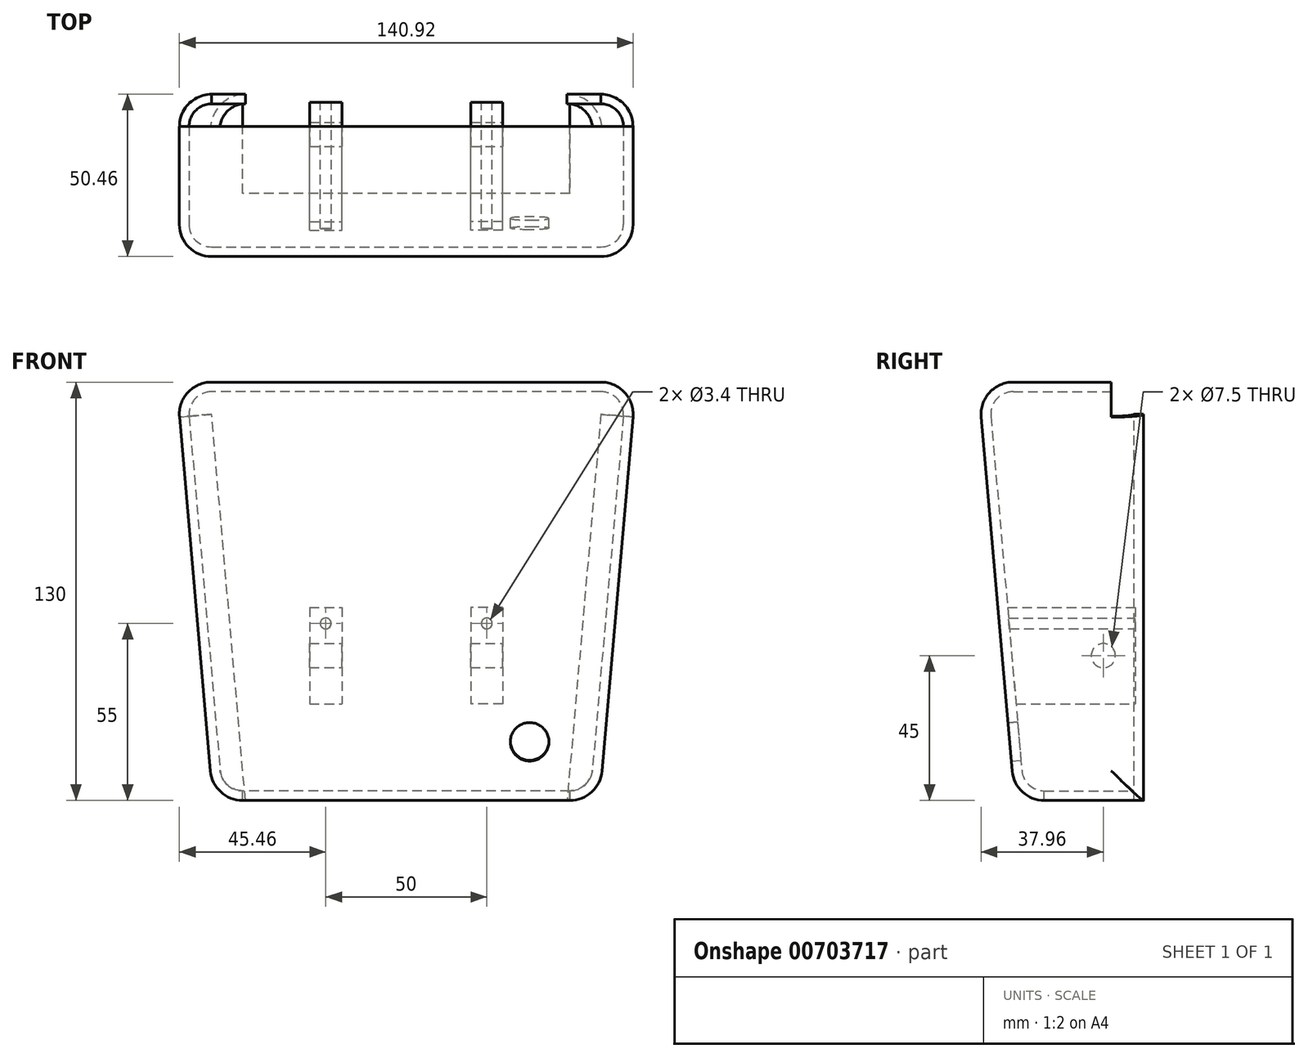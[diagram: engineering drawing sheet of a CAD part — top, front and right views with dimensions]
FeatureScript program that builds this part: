
annotation { "Feature Type Name" : "Feature", "Feature Type Description" : "" }
export const myFeature = defineFeature(function(context is Context, id is Id, definition is map)
    precondition{}
    {
        {
            var Q0;
            Q0=qCreatedBy(makeId("Top.planeOp"),FACE);
            var sketch = newSketch(context, id + "F0", { "sketchPlane" : qUnion([Q0])});
            skLineSegment(sketch, "E0.bottom", {"start": v(0, 0) * mm, "end": v(120, 0) * mm});
            skLineSegment(sketch, "E0.top", {"start": v(0, -40) * mm, "end": v(120, -40) * mm});
            skLineSegment(sketch, "E0.left", {"start": v(0, 0) * mm, "end": v(0, -40) * mm});
            skLineSegment(sketch, "E0.right", {"start": v(120, 0) * mm, "end": v(120, -40) * mm});
            skPoint(sketch, "E1", {"position": v(120, 0) * mm});
            skLineSegment(sketch, "E2", {"start": v(120, 0) * mm, "end": v(120, -47.34) * mm, "construction": true});
            skPoint(sketch, "E3.visualSharp", {"position": v(120, -40) * mm});
            skLineSegment(sketch, "E3.filletArc", {"start": v(120, -40) * mm, "end": v(120, -40) * mm});
            skLineSegment(sketch, "E4.filletArc", {"start": v(120, 0) * mm, "end": v(120, 0) * mm});
            skPoint(sketch, "E5.visualSharp", {"position": v(0, 0) * mm});
            skLineSegment(sketch, "E5.filletArc", {"start": v(0, 0) * mm, "end": v(0, 0) * mm});
            skPoint(sketch, "E6.visualSharp", {"position": v(0, -40) * mm});
            skLineSegment(sketch, "E6.filletArc", {"start": v(0, -40) * mm, "end": v(0, -40) * mm});
            skSolve(sketch);
        }
        {
            var Q0;
            Q0 = qSketchRegion(id + "F0", true);
            extrude(context, id + "F1", {"entities" : qUnion([Q0]), "depth" : 130 * mm, "offsetDistance" : 25 * mm, "hasDraft" : true, "draftAngle" : 5 * degree});
        }
        {
            var Q0;
            Q0=qCreatedBy(makeId("Front.planeOp"),FACE);
            var sketch = newSketch(context, id + "F2", { "sketchPlane" : qUnion([Q0])});
            skLineSegment(sketch, "E7.bottom", {"start": v(146.84, 147.54) * mm, "end": v(-36.23, 147.54) * mm});
            skLineSegment(sketch, "E7.top", {"start": v(146.84, -9) * mm, "end": v(-36.23, -9) * mm});
            skLineSegment(sketch, "E7.left", {"start": v(146.84, 147.54) * mm, "end": v(146.84, -9) * mm});
            skLineSegment(sketch, "E7.right", {"start": v(-36.23, 147.54) * mm, "end": v(-36.23, -9) * mm});
            skPoint(sketch, "E7.middle", {"position": v(55.3, 69.27) * mm});
            skSolve(sketch);
        }
        {
            var Q0;
            Q0=makeQuery(id+"F2.imprint","IMPRINT",FACE,{"disambiguationData":[TD([[makeQuery(id+"F2.imprint","IMPRINT",EDGE,{"derivedFrom":sQuery(id+"F2.wireOp",EDGE,"E7.bottom")}),1.0]])]});
            extrude(context, id + "F3", {"entities" : qUnion([Q0]), "operationType" : NewBodyOperationType.REMOVE, "oppositeDirection" : true, "depth" : 150 * mm, "offsetDistance" : 25 * mm});
        }
        {
            var Q0;
            Q0=makeQuery(id+"F1.opExtrude","SWEPT_FACE",FACE,{"disambiguationData":[OSD([sQuery(id+"F0.wireOp",EDGE,"E0.right")])]});
            var Q1;
            Q1=makeQuery(id+"F1.opExtrude","SWEPT_FACE",FACE,{"disambiguationData":[OSD([sQuery(id+"F0.wireOp",EDGE,"E0.left")])]});
            var Q2;
            Q2=makeQuery(id+"F1.opExtrude","CAP_FACE",FACE,{"disambiguationData":[OSD([sQuery(id+"F0.wireOp",EDGE,"E0.bottom"),sQuery(id+"F0.wireOp",EDGE,"E0.top"),sQuery(id+"F0.wireOp",EDGE,"E0.left"),sQuery(id+"F0.wireOp",EDGE,"E0.right")])],"isStart":false});
            var Q3;
            Q3=makeQuery(id+"F1.opExtrude","CAP_EDGE",EDGE,{"disambiguationData":[OSD([sQuery(id+"F0.wireOp",EDGE,"E0.bottom")])],"isStart":true});
            var Q4;
            Q4=makeQuery(id+"F1.opExtrude","SWEPT_FACE",FACE,{"disambiguationData":[OSD([sQuery(id+"F0.wireOp",EDGE,"E0.top")])]});
            fillet(context, id + "F4", {"entities" : qUnion([Q0, Q1, Q2, Q3, Q4]), "radius" : 10 * mm, "tangentPropagation" : true, "allowEdgeOverflow" : false});
        }
        {
            var Q0;
            Q0=makeQuery(id+"F3.boolean.opBoolean","COPY",FACE,{"derivedFrom":makeQuery(id+"F3.opExtrude","CAP_FACE",FACE,{"disambiguationData":[OSD([sQuery(id+"F2.wireOp",EDGE,"E7.bottom"),sQuery(id+"F2.wireOp",EDGE,"E7.top"),sQuery(id+"F2.wireOp",EDGE,"E7.left"),sQuery(id+"F2.wireOp",EDGE,"E7.right")])],"isStart":true})});
            var Q1;
            Q1=makeQuery(id+"F1.opExtrude","CAP_FACE",FACE,{"disambiguationData":[OSD([sQuery(id+"F0.wireOp",EDGE,"E0.bottom"),sQuery(id+"F0.wireOp",EDGE,"E0.top"),sQuery(id+"F0.wireOp",EDGE,"E0.left"),sQuery(id+"F0.wireOp",EDGE,"E0.right")])],"isStart":true});
            var Q2;
            Q2=makeQuery(id+"F4.opFillet","BLEND_FACE",FACE,{"disambiguationData":[OSD([sQuery(id+"F0.wireOp",EDGE,"E0.bottom")])]});
            shell(context, id + "F5", {"entities" : qUnion([Q0, Q1, Q2]), "thickness" : 3 * mm});
        }
        {
            var Q0;
            Q0=makeQuery(id+"F2.imprint","IMPRINT",FACE,{"disambiguationData":[TD([[makeQuery(id+"F2.imprint","IMPRINT",EDGE,{"derivedFrom":sQuery(id+"F2.wireOp",EDGE,"E7.bottom")}),1.0]])]});
            var sketch = newSketch(context, id + "F6", { "sketchPlane" : qUnion([Q0])});
            skLineSegment(sketch, "E8.bottom", {"start": v(0, 0) * mm, "end": v(120, 0) * mm, "construction": true});
            skLineSegment(sketch, "E8.top", {"start": v(0, 50) * mm, "end": v(120, 50) * mm, "construction": true});
            skLineSegment(sketch, "E8.left", {"start": v(0, 0) * mm, "end": v(0, 50) * mm, "construction": true});
            skLineSegment(sketch, "E8.right", {"start": v(120, 0) * mm, "end": v(120, 50) * mm, "construction": true});
            skLineSegment(sketch, "E9.bottom", {"start": v(120, 50) * mm, "end": v(90, 50) * mm, "construction": true});
            skLineSegment(sketch, "E9.top", {"start": v(120, 60) * mm, "end": v(90, 60) * mm, "construction": true});
            skLineSegment(sketch, "E9.left", {"start": v(120, 50) * mm, "end": v(120, 60) * mm, "construction": true});
            skLineSegment(sketch, "E9.right", {"start": v(90, 50) * mm, "end": v(90, 60) * mm, "construction": true});
            skLineSegment(sketch, "E10.bottom", {"start": v(0, 50) * mm, "end": v(30, 50) * mm, "construction": true});
            skLineSegment(sketch, "E10.top", {"start": v(0, 60) * mm, "end": v(30, 60) * mm, "construction": true});
            skLineSegment(sketch, "E10.left", {"start": v(0, 50) * mm, "end": v(0, 60) * mm, "construction": true});
            skLineSegment(sketch, "E10.right", {"start": v(30, 50) * mm, "end": v(30, 60) * mm, "construction": true});
            skLineSegment(sketch, "E11.bottom", {"start": v(30, 60) * mm, "end": v(40, 60) * mm});
            skLineSegment(sketch, "E11.top", {"start": v(30, 30) * mm, "end": v(40, 30) * mm});
            skLineSegment(sketch, "E11.left", {"start": v(30, 60) * mm, "end": v(30, 30) * mm});
            skLineSegment(sketch, "E11.right", {"start": v(40, 60) * mm, "end": v(40, 30) * mm});
            skLineSegment(sketch, "E12.bottom", {"start": v(90, 60) * mm, "end": v(80, 60) * mm});
            skLineSegment(sketch, "E12.top", {"start": v(90, 30) * mm, "end": v(80, 30) * mm});
            skLineSegment(sketch, "E12.left", {"start": v(90, 60) * mm, "end": v(90, 30) * mm});
            skLineSegment(sketch, "E12.right", {"start": v(80, 60) * mm, "end": v(80, 30) * mm});
            skLineSegment(sketch, "E13.bottom", {"start": v(40, 60) * mm, "end": v(35, 60) * mm, "construction": true});
            skLineSegment(sketch, "E13.top", {"start": v(40, 55) * mm, "end": v(35, 55) * mm, "construction": true});
            skLineSegment(sketch, "E13.left", {"start": v(40, 60) * mm, "end": v(40, 55) * mm, "construction": true});
            skLineSegment(sketch, "E13.right", {"start": v(35, 60) * mm, "end": v(35, 55) * mm, "construction": true});
            skCircle(sketch, "E14", {"center": v(35, 55) * mm, "radius": 1.7 * mm});
            skLineSegment(sketch, "E15.bottom", {"start": v(80, 60) * mm, "end": v(85, 60) * mm, "construction": true});
            skLineSegment(sketch, "E15.top", {"start": v(80, 55) * mm, "end": v(85, 55) * mm, "construction": true});
            skLineSegment(sketch, "E15.left", {"start": v(80, 60) * mm, "end": v(80, 55) * mm, "construction": true});
            skLineSegment(sketch, "E15.right", {"start": v(85, 60) * mm, "end": v(85, 55) * mm, "construction": true});
            skCircle(sketch, "E16", {"center": v(85, 55) * mm, "radius": 1.7 * mm});
            skSolve(sketch);
        }
        {
            var Q0;
            Q0 = qSketchRegion(id + "F6", true);
            extrude(context, id + "F7", {"entities" : qUnion([Q0]), "operationType" : NewBodyOperationType.ADD, "endBound" : BoundingType.UP_TO_NEXT, "depth" : 25 * mm, "offsetDistance" : 25 * mm, "hasSecondDirection" : true, "secondDirectionOppositeDirection" : false, "secondDirectionDepth" : 2.5 * mm});
        }
        {
            var Q0;
            Q0=makeQuery(id+"F7.opExtrude","SWEPT_FACE",FACE,{"disambiguationData":[OSD([sQuery(id+"F6.wireOp",EDGE,"E12.left")])]});
            var sketch = newSketch(context, id + "F8", { "sketchPlane" : qUnion([Q0])});
            skLineSegment(sketch, "E17", {"start": v(-2.5, 30) * mm, "end": v(-2.5, 45) * mm, "construction": true});
            skLineSegment(sketch, "E18", {"start": v(-2.5, 45) * mm, "end": v(-12.5, 45) * mm, "construction": true});
            skPoint(sketch, "E19", {"position": v(-12.5, 45) * mm});
            skSolve(sketch);
        }
        {
            var Q0;
            Q0=sQuery(id+"F8.wireOp",VERTEX,"E19");
            var Q1;
            Q1=makeQuery(id+"F1.opExtrude","SWEPT_BODY",BODY,{"disambiguationData":[OSD([sQuery(id+"F0.wireOp",EDGE,"E0.bottom"),sQuery(id+"F0.wireOp",EDGE,"E0.top"),sQuery(id+"F0.wireOp",EDGE,"E0.left"),sQuery(id+"F0.wireOp",EDGE,"E0.right")])]});
            hole(context, id + "F9", {"style" : HoleStyle.SIMPLE, "endStyle" : HoleEndStyle.BLIND, "holeDiameter" : 7.5 * mm, "majorDiameter" : 5 * mm, "holeDepth" : 60 * mm, "isTappedThrough" : true, "tappedDepth" : 12 * mm, "tapClearance" : 3, "startFromSketch" : true, "locations" : qUnion([Q0]), "scope" : qUnion([Q1])});
        }
        {
            var Q0;
            {var subQ0=sQuery(id+"F0.wireOp",EDGE,"E0.top");Q0=makeQuery(id+"F5.opShell","OFFSET_FACE",FACE,{"disambiguationData":[OSD([subQ0]),TDD([makeQuery(id+"F1.opExtrude","SWEPT_FACE",FACE,{"disambiguationData":[OSD([subQ0])]})])]});}
            var sketch = newSketch(context, id + "F10", { "sketchPlane" : qUnion([Q0])});
            skPoint(sketch, "E20", {"position": v(-98.33, 21.77) * mm});
            skSolve(sketch);
        }
        {
            var Q0;
            Q0=sQuery(id+"F10.wireOp",VERTEX,"E20");
            var Q1;
            Q1=makeQuery(id+"F1.opExtrude","SWEPT_BODY",BODY,{"disambiguationData":[OSD([sQuery(id+"F0.wireOp",EDGE,"E0.bottom"),sQuery(id+"F0.wireOp",EDGE,"E0.top"),sQuery(id+"F0.wireOp",EDGE,"E0.left"),sQuery(id+"F0.wireOp",EDGE,"E0.right")])]});
            hole(context, id + "F11", {"style" : HoleStyle.SIMPLE, "endStyle" : HoleEndStyle.THROUGH, "holeDiameter" : 12 * mm, "majorDiameter" : 5 * mm, "isTappedThrough" : true, "tappedDepth" : 12 * mm, "tapClearance" : 3, "locations" : qUnion([Q0]), "scope" : qUnion([Q1])});
        }
    });
